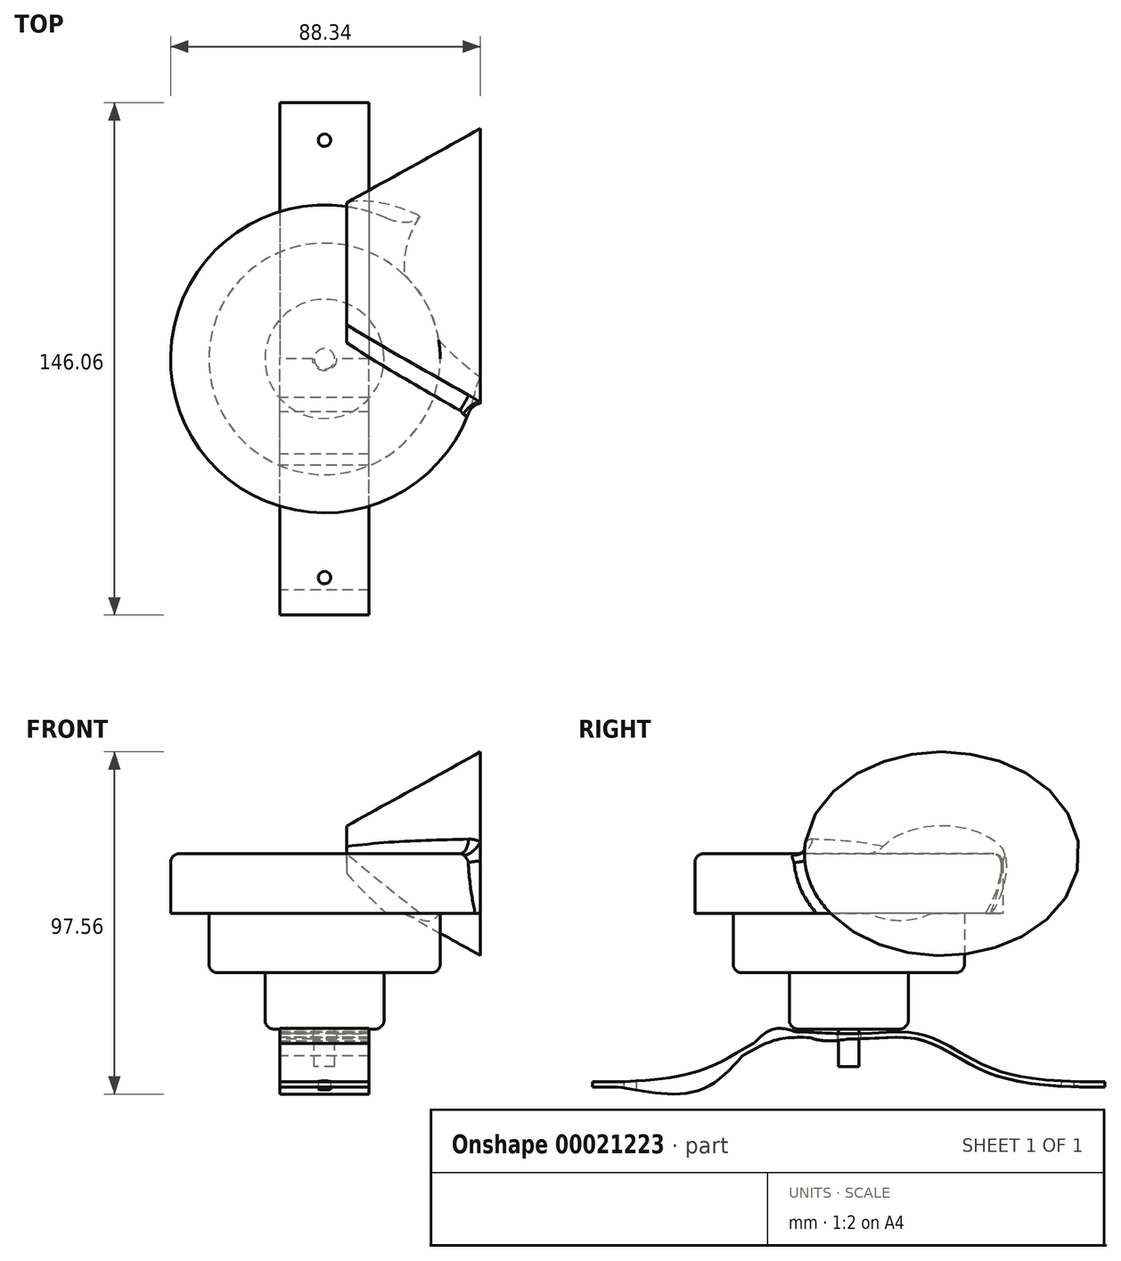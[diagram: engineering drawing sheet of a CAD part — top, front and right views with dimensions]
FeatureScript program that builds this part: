
annotation { "Feature Type Name" : "Feature", "Feature Type Description" : "" }
export const myFeature = defineFeature(function(context is Context, id is Id, definition is map)
    precondition{}
    {
        {
            var Q0;
            Q0=qCreatedBy(makeId("Right.planeOp"),FACE);
            var sketch = newSketch(context, id + "F0", { "sketchPlane" : qUnion([Q0])});
            skFitSpline(sketch, "E0", {"points": [v(-73.03, 0) * mm, v(-42.33, 3.14) * mm, v(-21.68, 13.15) * mm, v(0, 13.72) * mm], "startDerivative": vector(60.79, 0) * mm, "endDerivative": vector(95.06, 0) * mm});
            skFitSpline(sketch, "E1.0", {"points": [v(-73.03, 0) * mm, v(-65.52, 0) * mm, v(-40.79, -0.18) * mm, v(-21.89, 16.36) * mm, v(-9.84, 13.72) * mm, v(0, 13.72) * mm]});
            skLineSegment(sketch, "E2", {"start": v(-73.03, 0) * mm, "end": v(-73.03, 0) * mm});
            skLineSegment(sketch, "E3", {"start": v(0, 13.72) * mm, "end": v(0, 13.72) * mm});
            skLineSegment(sketch, "E4", {"start": v(0, 23.1) * mm, "end": v(0, -24.76) * mm, "construction": true});
            skFitSpline(sketch, "E5.MirrorCS", {"points": [v(73.03, 0) * mm, v(42.33, 3.14) * mm, v(21.68, 13.15) * mm, v(0, 13.72) * mm], "startDerivative": vector(-60.79, 0) * mm, "endDerivative": vector(-95.06, 0) * mm});
            skLineSegment(sketch, "E6.MirrorCS", {"start": v(73.03, 0) * mm, "end": v(73.03, 0) * mm});
            skFitSpline(sketch, "E7.0", {"points": [v(-73.03, 1.52) * mm, v(-70.49, 1.52) * mm, v(-65.73, 1.5) * mm, v(-58.5, 1.85) * mm, v(-53.85, 2.29) * mm, v(-50.18, 2.82) * mm, v(-47.48, 3.33) * mm, v(-45.32, 3.85) * mm, v(-43.65, 4.32) * mm, v(-42.03, 4.84) * mm, v(-40.1, 5.57) * mm, v(-37.14, 6.88) * mm, v(-33.69, 8.71) * mm, v(-30.45, 10.6) * mm, v(-27.93, 12.02) * mm, v(-26.06, 13) * mm, v(-24.18, 13.87) * mm, v(-22.6, 14.47) * mm, v(-21.3, 14.85) * mm, v(-20.02, 15.17) * mm, v(-18.4, 15.45) * mm, v(-16.44, 15.63) * mm, v(-13.77, 15.71) * mm, v(-10.25, 15.6) * mm, v(-5.55, 15.34) * mm, v(-1.95, 15.24) * mm, v(0, 15.24) * mm]});
            skFitSpline(sketch, "E8.0", {"points": [v(73.03, 1.52) * mm, v(70.49, 1.52) * mm, v(65.73, 1.5) * mm, v(58.5, 1.85) * mm, v(53.85, 2.29) * mm, v(50.18, 2.82) * mm, v(47.48, 3.33) * mm, v(45.32, 3.85) * mm, v(43.65, 4.32) * mm, v(42.03, 4.84) * mm, v(40.1, 5.57) * mm, v(37.14, 6.88) * mm, v(33.69, 8.71) * mm, v(30.45, 10.6) * mm, v(27.93, 12.02) * mm, v(26.06, 13) * mm, v(24.18, 13.87) * mm, v(22.6, 14.47) * mm, v(21.3, 14.85) * mm, v(20.02, 15.17) * mm, v(18.4, 15.45) * mm, v(16.44, 15.63) * mm, v(13.77, 15.71) * mm, v(10.25, 15.6) * mm, v(5.55, 15.34) * mm, v(1.95, 15.24) * mm, v(0, 15.24) * mm]});
            skLineSegment(sketch, "E9", {"start": v(73.03, 0) * mm, "end": v(73.03, 1.52) * mm});
            skLineSegment(sketch, "E10", {"start": v(-73.03, 0) * mm, "end": v(-73.03, 1.52) * mm});
            skLineSegment(sketch, "E11", {"start": v(-73.03, -5.79) * mm, "end": v(-47.62, -5.79) * mm, "construction": true});
            skSolve(sketch);
        }
        {
            var Q0;
            Q0 = qSketchRegion(id + "F0", true);
            extrude(context, id + "F1", {"entities" : qUnion([Q0]), "depth" : 25.4 * mm});
        }
        {
            var Q0;
            Q0=qCreatedBy(makeId("Top.planeOp"),FACE);
            var sketch = newSketch(context, id + "F2", { "sketchPlane" : qUnion([Q0])});
            skCircle(sketch, "E12", {"center": v(12.7, 0) * mm, "radius": 3.4 * mm});
            skLineSegment(sketch, "E13", {"start": v(12.7, 73.97) * mm, "end": v(12.7, -72.03) * mm, "construction": true});
            skCircle(sketch, "E14", {"center": v(12.7, 62.36) * mm, "radius": 1.78 * mm});
            skCircle(sketch, "E15.MirrorC", {"center": v(12.7, -62.36) * mm, "radius": 1.78 * mm});
            skSolve(sketch);
        }
        {
            var Q0;
            Q0 = qSketchRegion(id + "F2", true);
            var Q1;
            Q1=makeQuery(id+"F1.opExtrude","SWEPT_FACE",FACE,{"disambiguationData":[OSD([sQuery(id+"F0.wireOp",EDGE,"E7.0")])]});
            extrude(context, id + "F3", {"entities" : qUnion([Q0]), "operationType" : NewBodyOperationType.REMOVE, "endBoundEntityFace" : qUnion([Q1]), "depth" : 19.05 * mm, "hasSecondDirection" : true, "secondDirectionOppositeDirection" : true, "secondDirectionDepth" : 2.54 * mm});
        }
        {
            var Q0;
            Q0=qCreatedBy(makeId("Top.planeOp"),FACE);
            cPlane(context, id + "F4", {"entities" : qUnion([Q0]), "cplaneType" : CPlaneType.OFFSET, "offset" : 16.5 * mm, "width" : 152.4 * mm, "height" : 152.4 * mm});
        }
        {
            var Q0;
            Q0=qCreatedBy(id+"F4.planeOp",FACE);
            var sketch = newSketch(context, id + "F5", { "sketchPlane" : qUnion([Q0])});
            skCircle(sketch, "E16", {"center": v(12.7, 0) * mm, "radius": 2.92 * mm});
            skCircle(sketch, "E17", {"center": v(12.7, 0) * mm, "radius": 16.97 * mm});
            skSolve(sketch);
        }
        {
            var Q0;
            Q0=makeQuery(id+"F5.imprint","IMPRINT",FACE,{"disambiguationData":[TD([[makeQuery(id+"F5.imprint","IMPRINT",EDGE,{"derivedFrom":sQuery(id+"F5.wireOp",EDGE,"E16")}),1.0]])]});
            extrude(context, id + "F6", {"entities" : qUnion([Q0]), "oppositeDirection" : true, "depth" : 10.72 * mm});
        }
        {
            var Q0;
            Q0=makeQuery(id+"F5.imprint","IMPRINT",FACE,{"disambiguationData":[TD([[makeQuery(id+"F5.imprint","IMPRINT",EDGE,{"derivedFrom":sQuery(id+"F5.wireOp",EDGE,"E16")}),-1.0]])]});
            var Q1;
            Q1=makeQuery(id+"F5.imprint","IMPRINT",FACE,{"disambiguationData":[TD([[makeQuery(id+"F5.imprint","IMPRINT",EDGE,{"derivedFrom":sQuery(id+"F5.wireOp",EDGE,"E16")}),1.0]])]});
            extrude(context, id + "F7", {"entities" : qUnion([Q0, Q1]), "operationType" : NewBodyOperationType.ADD, "depth" : 16.08 * mm});
        }
        {
            var Q0;
            Q0=makeQuery(id+"F7.opExtrude","CAP_FACE",FACE,{"disambiguationData":[OSD([sQuery(id+"F5.wireOp",EDGE,"E17")])],"isStart":false});
            var sketch = newSketch(context, id + "F8", { "sketchPlane" : qUnion([Q0])});
            skCircle(sketch, "E18", {"center": v(12.7, 0) * mm, "radius": 32.98 * mm});
            skSolve(sketch);
        }
        {
            var Q0;
            Q0 = qSketchRegion(id + "F8", true);
            extrude(context, id + "F9", {"entities" : qUnion([Q0]), "operationType" : NewBodyOperationType.ADD, "depth" : 16.97 * mm});
        }
        {
            var Q0;
            Q0=makeQuery(id+"F9.opExtrude","CAP_FACE",FACE,{"disambiguationData":[OSD([sQuery(id+"F8.wireOp",EDGE,"E18")])],"isStart":false});
            var sketch = newSketch(context, id + "F10", { "sketchPlane" : qUnion([Q0])});
            skCircle(sketch, "E19", {"center": v(12.7, 0) * mm, "radius": 43.9 * mm});
            skSolve(sketch);
        }
        {
            var Q0;
            Q0 = qSketchRegion(id + "F10", true);
            extrude(context, id + "F11", {"entities" : qUnion([Q0]), "depth" : 16.97 * mm});
        }
        {
            var Q0;
            Q0=qCreatedBy(makeId("Right.planeOp"),FACE);
            cPlane(context, id + "F12", {"entities" : qUnion([Q0]), "cplaneType" : CPlaneType.OFFSET, "offset" : 57.15 * mm, "width" : 152.4 * mm, "height" : 152.4 * mm});
        }
        {
            var Q0;
            Q0=qCreatedBy(id+"F12.planeOp",FACE);
            var sketch = newSketch(context, id + "F13", { "sketchPlane" : qUnion([Q0])});
            skEllipse(sketch, "E20", {"center": v(26.51, 66.52) * mm, "majorRadius": 39.15 * mm, "minorRadius": 29.03 * mm, "majorAxis": v(1, 0)});
            skSolve(sketch);
        }
        {
            var Q0;
            Q0=makeQuery(id+"F13.imprint","IMPRINT",FACE,{"disambiguationData":[TD([[makeQuery(id+"F13.imprint","IMPRINT",EDGE,{"derivedFrom":sQuery(id+"F13.wireOp",EDGE,"E20")}),1.0]])]});
            extrude(context, id + "F14", {"entities" : qUnion([Q0]), "operationType" : NewBodyOperationType.ADD, "oppositeDirection" : true, "depth" : 38.1 * mm, "hasDraft" : true, "draftAngle" : 29 * degree, "draftPullDirection" : true});
        }
        {
            var Q0;
            Q0=makeQuery(id+"F11.opExtrude","CAP_EDGE",EDGE,{"disambiguationData":[OSD([sQuery(id+"F10.wireOp",EDGE,"E19")])],"isStart":false});
            var Q1;
            Q1=makeQuery(id+"F9.opExtrude","CAP_EDGE",EDGE,{"disambiguationData":[OSD([sQuery(id+"F8.wireOp",EDGE,"E18")])],"isStart":true});
            var Q2;
            Q2=makeQuery(id+"F9.opExtrude","CAP_EDGE",EDGE,{"disambiguationData":[OSD([sQuery(id+"F8.wireOp",EDGE,"E18")])],"isStart":false});
            var Q3;
            Q3=makeQuery(id+"F7.opExtrude","CAP_EDGE",EDGE,{"disambiguationData":[OSD([sQuery(id+"F5.wireOp",EDGE,"E17")])],"isStart":false});
            var Q4;
            Q4=makeQuery(id+"F7.opExtrude","CAP_EDGE",EDGE,{"disambiguationData":[OSD([sQuery(id+"F5.wireOp",EDGE,"E17")])],"isStart":true});
            fillet(context, id + "F15", {"entities" : qUnion([Q0, Q1, Q2, Q3, Q4]), "radius" : 2.54 * mm, "tangentPropagation" : true, "allowEdgeOverflow" : false});
        }
        {
            var Q0;
            Q0=makeQuery(id+"F14.boolean.opBoolean","INTERSECT",EDGE,{"derivedFrom":[makeQuery(id+"F11.opExtrude","CAP_FACE",FACE,{"disambiguationData":[OSD([sQuery(id+"F10.wireOp",EDGE,"E19")])],"isStart":false}),makeQuery(id+"F14.opExtrude","SWEPT_FACE",FACE,{"disambiguationData":[OSD([sQuery(id+"F13.wireOp",EDGE,"E20")])]})]});
            var Q1;
            Q1=makeQuery(id+"F14.boolean.opBoolean","INTERSECT",EDGE,{"disambiguationData":[OD(1.0)],"derivedFrom":[makeQuery(id+"F11.opExtrude","SWEPT_FACE",FACE,{"disambiguationData":[OSD([sQuery(id+"F10.wireOp",EDGE,"E19")])]}),makeQuery(id+"F14.opExtrude","SWEPT_FACE",FACE,{"disambiguationData":[OSD([sQuery(id+"F13.wireOp",EDGE,"E20")])]})]});
            fillet(context, id + "F16", {"entities" : qUnion([Q0, Q1]), "radius" : 5.08 * mm, "tangentPropagation" : true, "allowEdgeOverflow" : false});
        }
    });
